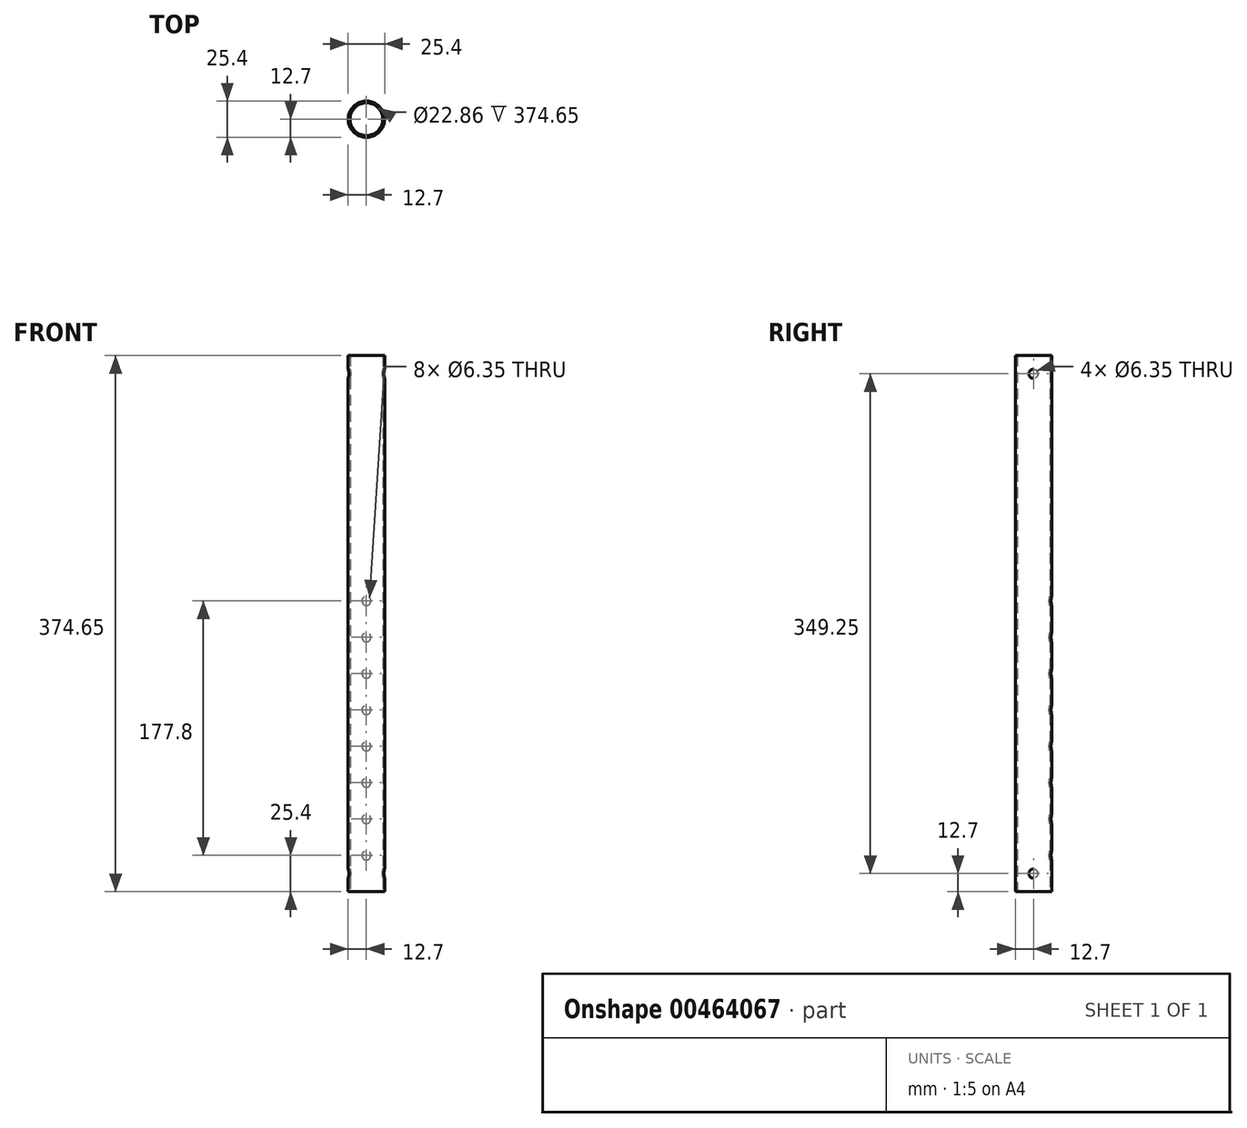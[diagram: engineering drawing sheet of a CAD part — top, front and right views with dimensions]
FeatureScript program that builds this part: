
annotation { "Feature Type Name" : "Feature", "Feature Type Description" : "" }
export const myFeature = defineFeature(function(context is Context, id is Id, definition is map)
    precondition{}
    {
        {
            var Q0;
            Q0=qCreatedBy(makeId("Top.planeOp"),FACE);
            var sketch = newSketch(context, id + "F0", { "sketchPlane" : qUnion([Q0])});
            skCircle(sketch, "E0", {"center": v(0, 0) * mm, "radius": 12.7 * mm});
            skSolve(sketch);
        }
        {
            var Q0;
            Q0=makeQuery(id+"F0.imprint","IMPRINT",FACE,{"disambiguationData":[TD([[makeQuery(id+"F0.imprint","IMPRINT",EDGE,{"derivedFrom":sQuery(id+"F0.wireOp",EDGE,"E0")}),1.0]])]});
            extrude(context, id + "F1", {"entities" : qUnion([Q0]), "depth" : 374.65 * mm});
        }
        {
            var Q0;
            Q0=qCreatedBy(makeId("Right.planeOp"),FACE);
            cPlane(context, id + "F2", {"entities" : qUnion([Q0]), "cplaneType" : CPlaneType.OFFSET, "offset" : 6.35 * mm, "width" : 152.4 * mm, "height" : 152.4 * mm});
        }
        {
            var Q0;
            Q0=qCreatedBy(id+"F2.planeOp",FACE);
            var sketch = newSketch(context, id + "F3", { "sketchPlane" : qUnion([Q0])});
            skLineSegment(sketch, "E1", {"start": v(0, 0) * mm, "end": v(0, 12.7) * mm});
            skLineSegment(sketch, "E2", {"start": v(0, 12.7) * mm, "end": v(0, 292.1) * mm});
            skCircle(sketch, "E3", {"center": v(0, 12.7) * mm, "radius": 3.18 * mm});
            skSolve(sketch);
        }
        {
            var Q0;
            Q0 = qSketchRegion(id + "F3", true);
            extrude(context, id + "F4", {"entities" : qUnion([Q0]), "operationType" : NewBodyOperationType.REMOVE, "depth" : 25.4 * mm, "hasSecondDirection" : true, "secondDirectionOppositeDirection" : true, "secondDirectionDepth" : 25.4 * mm});
        }
        {
            var Q0;
            Q0=qCreatedBy(id+"F2.planeOp",FACE);
            var sketch = newSketch(context, id + "F5", { "sketchPlane" : qUnion([Q0])});
            skLineSegment(sketch, "E4", {"start": v(0, 0) * mm, "end": v(0, 361.95) * mm});
            skCircle(sketch, "E5", {"center": v(0, 361.95) * mm, "radius": 3.18 * mm});
            skSolve(sketch);
        }
        {
            var Q0;
            Q0 = qSketchRegion(id + "F5", true);
            extrude(context, id + "F6", {"entities" : qUnion([Q0]), "operationType" : NewBodyOperationType.REMOVE, "depth" : 12.7 * mm, "hasSecondDirection" : true, "secondDirectionOppositeDirection" : true, "secondDirectionDepth" : 25.4 * mm});
        }
        {
            var Q0;
            Q0=makeQuery(id+"F1.opExtrude","CAP_FACE",FACE,{"disambiguationData":[OSD([sQuery(id+"F0.wireOp",EDGE,"E0")])],"isStart":true});
            var sketch = newSketch(context, id + "F7", { "sketchPlane" : qUnion([Q0])});
            skCircle(sketch, "E6", {"center": v(0, 0) * mm, "radius": 11.43 * mm});
            skSolve(sketch);
        }
        {
            var Q0;
            Q0=makeQuery(id+"F7.imprint","IMPRINT",FACE,{"disambiguationData":[TD([[makeQuery(id+"F7.imprint","IMPRINT",EDGE,{"derivedFrom":sQuery(id+"F7.wireOp",EDGE,"E6")}),1.0]])]});
            extrude(context, id + "F8", {"entities" : qUnion([Q0]), "operationType" : NewBodyOperationType.REMOVE, "oppositeDirection" : true, "depth" : 603.25 * mm, "offsetDistance" : 25.4 * mm});
        }
        {
            var Q0;
            Q0=qCreatedBy(makeId("Front.planeOp"),FACE);
            var sketch = newSketch(context, id + "F9", { "sketchPlane" : qUnion([Q0])});
            skLineSegment(sketch, "E7", {"start": v(0, 0) * mm, "end": v(0, 25.4) * mm});
            skLineSegment(sketch, "E8", {"start": v(0, 25.4) * mm, "end": v(0, 50.8) * mm});
            skLineSegment(sketch, "E9", {"start": v(0, 50.8) * mm, "end": v(0, 76.2) * mm});
            skLineSegment(sketch, "E10", {"start": v(0, 76.2) * mm, "end": v(0, 101.6) * mm});
            skLineSegment(sketch, "E11", {"start": v(0, 101.6) * mm, "end": v(0, 127) * mm});
            skLineSegment(sketch, "E12", {"start": v(0, 127) * mm, "end": v(0, 152.4) * mm});
            skLineSegment(sketch, "E13", {"start": v(0, 152.4) * mm, "end": v(0, 177.8) * mm});
            skLineSegment(sketch, "E14", {"start": v(0, 177.8) * mm, "end": v(0, 203.2) * mm});
            skCircle(sketch, "E15", {"center": v(0, 203.2) * mm, "radius": 3.18 * mm});
            skCircle(sketch, "E16", {"center": v(0, 177.8) * mm, "radius": 3.18 * mm});
            skCircle(sketch, "E17", {"center": v(0, 152.4) * mm, "radius": 3.18 * mm});
            skCircle(sketch, "E18", {"center": v(0, 127) * mm, "radius": 3.18 * mm});
            skCircle(sketch, "E19", {"center": v(0, 101.6) * mm, "radius": 3.18 * mm});
            skCircle(sketch, "E20", {"center": v(0, 76.2) * mm, "radius": 3.18 * mm});
            skCircle(sketch, "E21", {"center": v(0, 50.8) * mm, "radius": 3.18 * mm});
            skCircle(sketch, "E22", {"center": v(0, 25.4) * mm, "radius": 3.18 * mm});
            skSolve(sketch);
        }
        {
            var Q0;
            Q0 = qSketchRegion(id + "F9", true);
            extrude(context, id + "F10", {"entities" : qUnion([Q0]), "operationType" : NewBodyOperationType.REMOVE, "oppositeDirection" : true, "depth" : 25.4 * mm, "offsetDistance" : 25.4 * mm});
        }
    });
